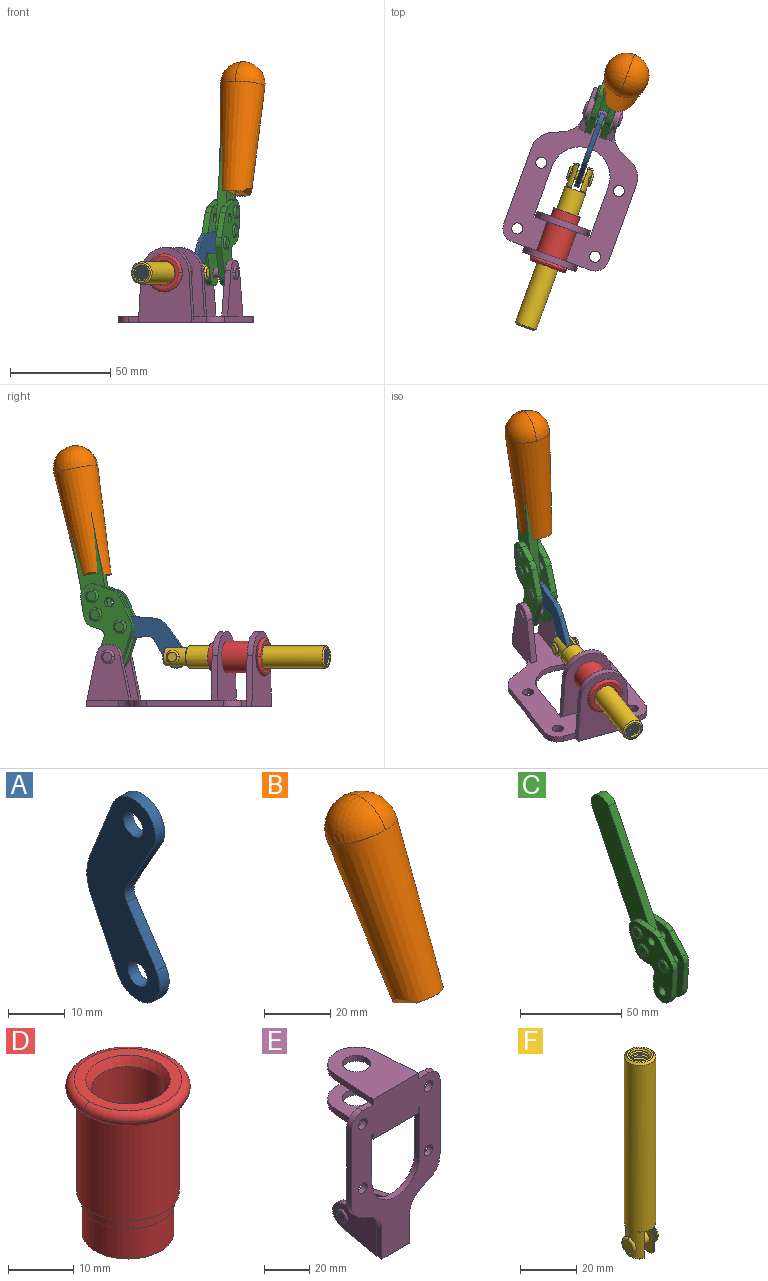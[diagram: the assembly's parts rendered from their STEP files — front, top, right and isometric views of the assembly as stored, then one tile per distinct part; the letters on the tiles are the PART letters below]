
ASSEMBLY  parts=6 mates=6
PART A: 12 faces, bbox 2.3x18.2x42.8 mm
  f0: cylinder r=2.4mm len=4.8mm, axis (1,0,0), area 34.9mm2, adj f4,f11
  f1: cylinder r=10.41mm len=8.47mm, axis (1,0,0), area 20.2mm2, adj f4,f9,f10,f11
  f2: cylinder r=3.05mm len=3.16mm, axis (1,0,0), area 7.7mm2, adj f4,f6,f7,f11
  f3: cylinder r=2.4mm len=4.8mm, axis (1,0,0), area 34.9mm2, adj f4,f11
  f4: plane 42.81x18.23mm, normal (-1,0,0), area 414.1mm2, adj f0,f1,f2,f3,f5,f6,f7,f8
  f5: cylinder r=5.54mm len=10.67mm, axis (1,0,0), area 41.8mm2, adj f4,f6,f10,f11
  f6: plane 11.66x6.53mm, normal (0,-0.87,-0.49), area 30.9mm2, adj f2,f4,f5,f11
  f7: plane 11.17x7.33mm, normal (0,-0.84,0.55), area 30.9mm2, adj f2,f4,f8,f11
  f8: cylinder r=5.54mm len=10.51mm, axis (1,0,0), area 41.8mm2, adj f4,f7,f9,f11
  f9: plane 13.67x6.67mm, normal (0,0.9,-0.44), area 35.1mm2, adj f1,f4,f8,f11
  f10: plane 14.1x5.7mm, normal (0,0.93,0.37), area 35.1mm2, adj f1,f4,f5,f11
  f11: plane 42.81x18.23mm, normal (1,0,0), area 414.1mm2, adj f0,f1,f2,f3,f5,f6,f7,f8
PART B: 11 faces, bbox 22.3x42.6x64.5 mm
  f0: sphere r=11.13mm, area 411.4mm2, adj f1,f8
  f1: cone r=11.11mm half-angle=3.3deg, axis (0,0.44,0.9), area 3251.8mm2, adj f0,f7,f8,f9,f10
  f2: cylinder r=6.16mm len=11.7mm, axis (1,0,0), area 89.5mm2, adj f3,f4,f5,f6
  f3: plane 60.23x36.75mm, normal (-1,0,0), area 763.6mm2, adj f2,f4,f6,f10
  f4: plane 51.37x25.05mm, normal (0,0.9,-0.44), area 264.2mm2, adj f2,f3,f5,f10
  f5: plane 60.23x36.75mm, normal (1,0,0), area 763.6mm2, adj f2,f4,f6,f10
  f6: plane 51.37x25.05mm, normal (0,-0.9,0.44), area 264.2mm2, adj f2,f3,f5,f10
  f7: plane 9.95x5.95mm, normal (0.71,-0.31,-0.64), area 25.8mm2, adj f1,f10
  f8: sphere r=11.13mm, area 411.4mm2, adj f0,f1
  f9: plane 9.95x5.95mm, normal (-0.71,-0.31,-0.64), area 25.8mm2, adj f1,f10
  f10: plane 14.27x11.38mm, normal (0,-0.44,-0.9), area 106.7mm2, adj f1,f3,f4,f5,f6,f7,f9
PART C: 59 faces, bbox 12.9x60.2x99.6 mm
  f0: torus R=2.39mm, axis (-1,0,0), area 14.9mm2, adj f20,f43,f51
  f1: torus R=2.39mm, axis (-1,0,0), area 14.9mm2, adj f19,f42,f51
  f2: torus R=2.39mm, axis (-1,0,0), area 14.9mm2, adj f18,f35,f51
  f3: torus R=2.39mm, axis (-1,0,0), area 14.9mm2, adj f14,f17,f23
  f4: torus R=2.39mm, axis (-1,0,0), area 14.9mm2, adj f13,f16,f23
  f5: torus R=2.39mm, axis (-1,0,0), area 14.9mm2, adj f12,f15,f23
  f6: cylinder r=2.39mm len=4.78mm, axis (1,0,0), area 46.5mm2, adj f48,f50,f51
  f7: cylinder r=2.39mm len=4.78mm, axis (1,0,0), area 46.5mm2, adj f50,f51
  f8: cylinder r=6.35mm len=12.68mm, axis (1,0,0), area 61.8mm2, adj f38,f39,f50,f51
  f9: cylinder r=2.39mm len=4.78mm, axis (-1,0,0), area 70.5mm2, adj f46,f50
  f10: cylinder r=2.39mm len=4.78mm, axis (-1,0,0), area 46.5mm2, adj f23,f45,f46
  f11: cylinder r=2.39mm len=4.78mm, axis (-1,0,0), area 46.5mm2, adj f23,f46
  f12: plane 4.78x4.78mm, normal (1,0,0), area 17.9mm2, adj f5,f15
  f13: plane 4.78x4.78mm, normal (1,0,0), area 17.9mm2, adj f4,f16
  f14: plane 4.78x4.78mm, normal (1,0,0), area 17.9mm2, adj f3,f17
  f15: torus R=2.39mm, axis (-1,0,0), area 14.9mm2, adj f5,f12,f23
  f16: torus R=2.39mm, axis (-1,0,0), area 14.9mm2, adj f4,f13,f23
  f17: torus R=2.39mm, axis (-1,0,0), area 14.9mm2, adj f3,f14,f23
  f18: plane 4.78x4.78mm, normal (-1,0,0), area 17.9mm2, adj f2,f35
  f19: plane 4.78x4.78mm, normal (-1,0,0), area 17.9mm2, adj f1,f42
  f20: plane 4.78x4.78mm, normal (-1,0,0), area 17.9mm2, adj f0,f43
  f21: plane 2.26x0.2mm, normal (1,0,0), area 0.2mm2, adj f31,f44
  f22: plane 2.26x0.2mm, normal (-1,0,0), area 0.2mm2, adj f41,f44
  f23: plane 39.37x30.77mm, normal (1,0,0), area 565.5mm2, adj f3,f4,f5,f10,f11,f15,f16,f17
  f24: cylinder r=6.1mm len=4.15mm, axis (-1,0,0), area 14.7mm2, adj f23,f25,f32,f46
  f25: plane 10.25x9.01mm, normal (0,-0.75,0.66), area 42.3mm2, adj f23,f24,f26,f46
  f26: cylinder r=6.35mm len=4.64mm, axis (-1,0,0), area 15.6mm2, adj f23,f25,f27,f46
  f27: plane 15.84x3.1mm, normal (0,-1,-0.07), area 49.2mm2, adj f23,f26,f28,f46
  f28: cylinder r=6.35mm len=12.68mm, axis (-1,0,0), area 61.8mm2, adj f23,f27,f29,f46
  f29: plane 8.11x3.1mm, normal (0,1,0.07), area 25.2mm2, adj f23,f28,f30,f46
  f30: cylinder r=3.05mm len=3.25mm, axis (-1,0,0), area 14.8mm2, adj f23,f29,f31,f46
  f31: plane 5.99x3.1mm, normal (0,0.07,-1), area 18.6mm2, adj f21,f23,f30,f44,f46
  f32: plane 9.5x3.1mm, normal (0,-0.07,1), area 29.5mm2, adj f23,f24,f33,f46,f47
  f33: cylinder r=6.1mm len=8.63mm, axis (-1,0,0), area 39.1mm2, adj f23,f32,f34,f47
  f34: plane 8.65x3.96mm, normal (0,0.91,-0.42), area 29.5mm2, adj f23,f33,f44,f47
  f35: torus R=2.39mm, axis (-1,0,0), area 14.9mm2, adj f2,f18,f51
  f36: plane 10.25x9.01mm, normal (0,-0.75,0.66), area 42.3mm2, adj f37,f49,f50,f51
  f37: cylinder r=6.35mm len=4.64mm, axis (1,0,0), area 15.6mm2, adj f36,f38,f50,f51
  f38: plane 15.84x3.1mm, normal (0,-1,-0.07), area 49.2mm2, adj f8,f37,f50,f51
  f39: plane 8.11x3.1mm, normal (0,1,0.07), area 25.2mm2, adj f8,f40,f50,f51
  f40: cylinder r=3.05mm len=3.25mm, axis (1,0,0), area 14.8mm2, adj f39,f41,f50,f51
  f41: plane 5.99x3.1mm, normal (0,0.07,-1), area 18.6mm2, adj f22,f40,f44,f50,f51
  f42: torus R=2.39mm, axis (-1,0,0), area 14.9mm2, adj f1,f19,f51
  f43: torus R=2.39mm, axis (-1,0,0), area 14.9mm2, adj f0,f20,f51
  f44: cylinder r=6.35mm len=12.12mm, axis (-1,0,0), area 128.9mm2, adj f21,f22,f23,f31,f34,f41,f46,f47
  f45: plane 2.65x1.35mm, normal (1,0,0), area 1mm2, adj f10,f55
  f46: plane 39.08x20.42mm, normal (-1,0,0), area 412.5mm2, adj f9,f10,f11,f24,f25,f26,f27,f28
  f47: plane 77.62x39.82mm, normal (1,0,0), area 850mm2, adj f32,f33,f34,f44,f53,f54,f55
  f48: plane 2.65x1.35mm, normal (-1,0,0), area 1mm2, adj f6,f55
  f49: cylinder r=6.1mm len=4.15mm, axis (1,0,0), area 14.7mm2, adj f36,f50,f51,f56
  f50: plane 39.08x20.42mm, normal (1,0,0), area 412.5mm2, adj f6,f7,f8,f9,f36,f37,f38,f39
  f51: plane 39.37x30.77mm, normal (-1,0,0), area 565.5mm2, adj f0,f1,f2,f6,f7,f8,f35,f36
  f52: plane 8.65x3.96mm, normal (0,0.91,-0.42), area 29.5mm2, adj f44,f51,f57,f58
  f53: plane 68.49x33.4mm, normal (0,0.9,-0.44), area 358.1mm2, adj f44,f47,f54,f58
  f54: cylinder r=6.35mm len=12.06mm, axis (1,0,0), area 93.7mm2, adj f47,f53,f55,f58
  f55: plane 68.49x33.4mm, normal (0,-0.9,0.44), area 358.1mm2, adj f44,f45,f46,f47,f48,f50,f54,f58
  f56: plane 9.5x3.1mm, normal (0,-0.07,1), area 29.5mm2, adj f49,f50,f51,f57,f58
  f57: cylinder r=6.1mm len=8.63mm, axis (1,0,0), area 39.1mm2, adj f51,f52,f56,f58
  f58: plane 77.62x39.82mm, normal (-1,0,0), area 850mm2, adj f44,f52,f53,f54,f55,f56,f57
PART D: 15 faces, bbox 20.6x20.6x28.7 mm
  f0: torus R=8.26mm, axis (0,0,1), area 56.8mm2, adj f1,f10,f12
  f1: torus R=8.26mm, axis (0,0,1), area 56.8mm2, adj f0,f6,f13
  f2: cylinder r=5.59mm len=25.91mm, axis (0,0,1), area 909.6mm2, adj f3,f4
  f3: cone r=6.86mm half-angle=45deg, axis (0,0,-1), area 70.2mm2, adj f2,f14
  f4: cone r=6.47mm half-angle=30deg, axis (0,0,1), area 66.7mm2, adj f2,f13
  f5: cylinder r=7.04mm len=14.07mm, axis (0,0,1), area 252.6mm2, adj f11,f14
  f6: torus R=8.26mm, axis (0,0,1), area 56.8mm2, adj f1,f12,f13
  f7: cylinder r=7.16mm len=14.33mm, axis (0,0,1), area 91.5mm2, adj f9,f11
  f8: cylinder r=7.86mm len=18.42mm, axis (0,0,1), area 909.6mm2, adj f9,f10
  f9: plane 15.72x15.72mm, normal (0,0,-1), area 33mm2, adj f7,f8
  f10: plane 16.51x16.51mm, normal (0,0,-1), area 19.9mm2, adj f0,f8,f12
  f11: plane 14.33x14.33mm, normal (0,0,-1), area 5.7mm2, adj f5,f7
  f12: torus R=8.26mm, axis (0,0,1), area 56.8mm2, adj f0,f6,f10
  f13: plane 16.51x16.51mm, normal (0,0,1), area 82.7mm2, adj f1,f4,f6
  f14: plane 14.07x14.07mm, normal (0,0,-1), area 7.8mm2, adj f3,f5
PART E: 55 faces, bbox 55.7x37.4x89.8 mm
  f0: torus R=2.41mm, axis (-1,0,0), area 15mm2, adj f11,f15,f25
  f1: torus R=2.41mm, axis (-1,0,0), area 15mm2, adj f10,f12,f22
  f2: cylinder r=2.78mm len=5.56mm, axis (0,-1,0), area 54.2mm2, adj f30,f54
  f3: cylinder r=14.99mm len=29.97mm, axis (0,-1,0), area 145.9mm2, adj f30,f49,f53,f54
  f4: cylinder r=2.78mm len=5.56mm, axis (0,-1,0), area 54.2mm2, adj f30,f54
  f5: cylinder r=2.78mm len=5.56mm, axis (0,-1,0), area 54.2mm2, adj f30,f54
  f6: cylinder r=2.78mm len=5.56mm, axis (0,-1,0), area 54.2mm2, adj f30,f54
  f7: cylinder r=6.35mm len=12.7mm, axis (0,0,1), area 123.6mm2, adj f27,f51
  f8: cylinder r=6.35mm len=12.7mm, axis (0,0,-1), area 124.7mm2, adj f21,f35
  f9: cylinder r=2.41mm len=11.18mm, axis (-1,0,0), area 169.4mm2, adj f16,f19
  f10: plane 4.83x4.83mm, normal (1,0,0), area 18.3mm2, adj f1,f12
  f11: plane 4.83x4.83mm, normal (-1,0,0), area 18.3mm2, adj f0,f15
  f12: torus R=2.41mm, axis (-1,0,0), area 15mm2, adj f1,f10,f22
  f13: cylinder r=6.35mm len=12.41mm, axis (1,0,0), area 53.4mm2, adj f18,f19,f22,f23
  f14: cylinder r=6.35mm len=12.41mm, axis (-1,0,0), area 53.4mm2, adj f16,f17,f24,f25
  f15: torus R=2.41mm, axis (-1,0,0), area 15mm2, adj f0,f11,f25
  f16: plane 27.86x22.35mm, normal (1,0,0), area 425.4mm2, adj f9,f14,f17,f24,f30
  f17: plane 22.86x4.97mm, normal (0,0.21,0.98), area 72.5mm2, adj f14,f16,f25,f30
  f18: plane 22.86x4.97mm, normal (0,0.21,0.98), area 72.5mm2, adj f13,f19,f22,f30
  f19: plane 27.86x22.35mm, normal (-1,0,0), area 425.4mm2, adj f9,f13,f18,f23,f30
  f20: cylinder r=12.7mm len=25.35mm, axis (0,0,-1), area 119.8mm2, adj f21,f34,f35,f36
  f21: plane 34.21x28.07mm, normal (0,0,-1), area 702.4mm2, adj f8,f20,f30,f34,f36
  f22: plane 27.96x22.45mm, normal (1,0,0), area 407.2mm2, adj f1,f12,f13,f18,f23,f30,f42,f43
  f23: plane 22.86x4.97mm, normal (0,0.21,-0.98), area 72.5mm2, adj f13,f19,f22,f44
  f24: plane 22.86x4.97mm, normal (0,0.21,-0.98), area 72.5mm2, adj f14,f16,f25,f44
  f25: plane 27.86x22.35mm, normal (-1,0,0), area 407.1mm2, adj f0,f14,f15,f17,f24,f30,f45,f46
  f26: plane 3.1x0.95mm, normal (0,0,-1), area 2.7mm2, adj f30,f49,f50,f54
  f27: plane 34.21x28.07mm, normal (0,0,1), area 702.4mm2, adj f7,f28,f30,f50,f52
  f28: cylinder r=12.7mm len=25.35mm, axis (0,0,1), area 118.8mm2, adj f27,f50,f51,f52
  f29: plane 3.1x0.95mm, normal (0,0,-1), area 2.7mm2, adj f30,f52,f53,f54
  f30: plane 86.54x55.63mm, normal (0,1,0), area 2362.9mm2, adj f2,f3,f4,f5,f6,f16,f17,f18
  f31: plane 40.56x3.1mm, normal (-1,0,0), area 125.7mm2, adj f30,f32,f48,f54
  f32: cylinder r=7.11mm len=7.11mm, axis (0,-1,0), area 34.6mm2, adj f30,f31,f33,f54
  f33: plane 6.67x3.1mm, normal (0,0,1), area 20.4mm2, adj f30,f32,f34,f54
  f34: plane 25.39x3.13mm, normal (-1,0.06,0), area 79.5mm2, adj f20,f21,f33,f35,f54
  f35: plane 37.31x28.45mm, normal (0,0,1), area 789.9mm2, adj f8,f20,f34,f36,f54
  f36: plane 25.39x3.13mm, normal (1,0.06,0), area 79.5mm2, adj f20,f21,f35,f37,f54
  f37: plane 6.67x3.1mm, normal (0,0,1), area 20.4mm2, adj f30,f36,f38,f54
  f38: cylinder r=7.11mm len=7.11mm, axis (0,-1,0), area 34.6mm2, adj f30,f37,f39,f54
  f39: plane 40.56x3.1mm, normal (1,0,0), area 125.7mm2, adj f30,f38,f40,f54
  f40: cylinder r=11.18mm len=10.16mm, axis (0,-1,0), area 39.5mm2, adj f30,f39,f41,f54
  f41: plane 6.09x3.1mm, normal (0.42,0,-0.91), area 20.8mm2, adj f30,f40,f42,f54
  f42: cylinder r=11.18mm len=9.41mm, axis (0,-1,0), area 37.2mm2, adj f22,f30,f41,f43,f54
  f43: plane 16.5x3.1mm, normal (1,0,0), area 51.1mm2, adj f22,f42,f44,f54
  f44: plane 17.37x3.1mm, normal (0,0,-1), area 53.8mm2, adj f23,f24,f30,f43,f45,f54
  f45: plane 16.5x3.1mm, normal (-1,0,0), area 51.1mm2, adj f25,f44,f46,f54
  f46: cylinder r=11.18mm len=9.41mm, axis (0,-1,0), area 37.2mm2, adj f25,f30,f45,f47,f54
  f47: plane 6.09x3.1mm, normal (-0.42,0,-0.91), area 20.8mm2, adj f30,f46,f48,f54
  f48: cylinder r=11.18mm len=10.16mm, axis (0,-1,0), area 39.5mm2, adj f30,f31,f47,f54
  f49: plane 26.54x3.1mm, normal (-1,0,0), area 82.3mm2, adj f3,f26,f30,f54
  f50: plane 25.39x3.1mm, normal (1,0.06,0), area 78.8mm2, adj f26,f27,f28,f51,f54
  f51: plane 37.31x28.45mm, normal (0,0,-1), area 789.9mm2, adj f7,f28,f50,f52,f54
  f52: plane 25.39x3.1mm, normal (-1,0.06,0), area 78.8mm2, adj f27,f28,f29,f51,f54
  f53: plane 26.54x3.1mm, normal (1,0,0), area 82.3mm2, adj f3,f29,f30,f54
  f54: plane 89.66x55.63mm, normal (0,-1,0), area 2678.5mm2, adj f2,f3,f4,f5,f6,f26,f29,f31
PART F: 48 faces, bbox 12.6x11.1x86.1 mm
  f0: torus R=2.41mm, axis (-1,0,0), area 15mm2, adj f30,f32,f34
  f1: torus R=2.41mm, axis (-1,0,0), area 15mm2, adj f29,f31,f33
  f2: cylinder r=5.54mm len=72.39mm, axis (0,0,1), area 2518.5mm2, adj f3,f4,f42,f43
  f3: cone r=5.54mm half-angle=45deg, axis (0,0,1), area 7.6mm2, adj f2,f5,f41
  f4: cone r=5.54mm half-angle=45deg, axis (0,0,-1), area 34.9mm2, adj f2,f39
  f5: cylinder r=5.08mm len=11.48mm, axis (0,0,1), area 108.3mm2, adj f3,f7,f8,f41
  f6: cylinder r=2.41mm len=4.83mm, axis (-1,0,0), area 71.2mm2, adj f40,f41
  f7: cylinder r=2.41mm len=4.83mm, axis (-1,0,0), area 7.6mm2, adj f5,f34
  f8: cone r=5.08mm half-angle=45deg, axis (0,0,1), area 10.6mm2, adj f5,f37,f41
  f9: cone r=3.98mm half-angle=45deg, axis (0,0,1), area 17.6mm2, adj f27,f39,f45,f46,f47
  f10: cylinder r=2.41mm len=4.83mm, axis (-1,0,0), area 7.6mm2, adj f33,f38
  f11: cylinder r=3.2mm len=6.4mm, axis (0,0,1), area 78.4mm2, adj f12,f28,f44,f45,f47
  f12: cylinder r=3.2mm len=6.4mm, axis (0,0,1), area 10.5mm2, adj f11,f13,f45,f47
  f13: cylinder r=3.2mm len=6.4mm, axis (0,0,1), area 10.5mm2, adj f12,f14,f45,f47
  f14: cylinder r=3.2mm len=6.4mm, axis (0,0,1), area 10.5mm2, adj f13,f15,f45,f47
  f15: cylinder r=3.2mm len=6.4mm, axis (0,0,1), area 10.5mm2, adj f14,f16,f45,f47
  f16: cylinder r=3.2mm len=6.4mm, axis (0,0,1), area 10.5mm2, adj f15,f17,f45,f47
  f17: cylinder r=3.2mm len=6.4mm, axis (0,0,1), area 10.5mm2, adj f16,f18,f45,f47
  f18: cylinder r=3.2mm len=6.4mm, axis (0,0,1), area 10.5mm2, adj f17,f19,f45,f47
  f19: cylinder r=3.2mm len=6.4mm, axis (0,0,1), area 10.5mm2, adj f18,f20,f45,f47
  f20: cylinder r=3.2mm len=6.4mm, axis (0,0,1), area 10.5mm2, adj f19,f21,f45,f47
  f21: cylinder r=3.2mm len=6.4mm, axis (0,0,1), area 10.5mm2, adj f20,f22,f45,f47
  f22: cylinder r=3.2mm len=6.4mm, axis (0,0,1), area 10.5mm2, adj f21,f23,f45,f47
  f23: cylinder r=3.2mm len=6.4mm, axis (0,0,1), area 10.5mm2, adj f22,f24,f45,f47
  f24: cylinder r=3.2mm len=6.4mm, axis (0,0,1), area 10.5mm2, adj f23,f25,f45,f47
  f25: cylinder r=3.2mm len=6.4mm, axis (0,0,1), area 10.5mm2, adj f24,f26,f45,f47
  f26: cylinder r=3.2mm len=6.4mm, axis (0,0,1), area 10.5mm2, adj f25,f27,f45,f47
  f27: cylinder r=3.2mm len=6.4mm, axis (0,0,1), area 7.4mm2, adj f9,f26,f45,f47
  f28: cone r=3.2mm half-angle=60deg, axis (0,0,1), area 37.2mm2, adj f11
  f29: plane 4.83x4.83mm, normal (-1,0,0), area 18.3mm2, adj f1,f31
  f30: plane 4.83x4.83mm, normal (1,0,0), area 18.3mm2, adj f0,f32
  f31: torus R=2.41mm, axis (-1,0,0), area 15mm2, adj f1,f29,f33
  f32: torus R=2.41mm, axis (-1,0,0), area 15mm2, adj f0,f30,f34
  f33: plane 6.83x6.83mm, normal (1,0,0), area 18.3mm2, adj f1,f10,f31
  f34: plane 6.83x6.83mm, normal (-1,0,0), area 18.3mm2, adj f0,f7,f32
  f35: cone r=5.08mm half-angle=45deg, axis (0,0,1), area 10.6mm2, adj f36,f38,f40
  f36: plane 7.25x1.97mm, normal (0,0,-1), area 10mm2, adj f35,f40
  f37: plane 7.25x1.97mm, normal (0,0,-1), area 10mm2, adj f8,f41
  f38: cylinder r=5.08mm len=11.48mm, axis (0,0,1), area 108.3mm2, adj f10,f35,f40,f42
  f39: plane 9.55x9.55mm, normal (0,0,1), area 22mm2, adj f4,f9
  f40: plane 12.76x10.09mm, normal (1,0,0), area 95.7mm2, adj f6,f35,f36,f38,f42,f43
  f41: plane 12.76x10.09mm, normal (-1,0,0), area 95.7mm2, adj f3,f5,f6,f8,f37,f43
  f42: cone r=5.54mm half-angle=45deg, axis (0,0,1), area 7.6mm2, adj f2,f38,f40
  f43: plane 11.07x4.7mm, normal (0,0,-1), area 50.4mm2, adj f2,f40,f41
  f44: plane 0.89x0.62mm, normal (-1,0,0), area 0.3mm2, adj f11,f45,f46,f47
  f45: bspline ~24.8x7.63mm, area 266.6mm2, adj f9,f11,f12,f13,f14,f15,f16,f17
  f46: bspline ~24.87x7.63mm, area 73.6mm2, adj f9,f44,f45,f47
  f47: bspline ~24.98x7.63mm, area 272.5mm2, adj f9,f11,f12,f13,f14,f15,f16,f17
PLACE A rot(axis=(0.09,0.53,0.85),163deg) t=(31.71,29.07,7.7)mm
PLACE B rot(axis=(0.59,-0.1,-0.8),25deg) t=(27.91,5.01,46.24)mm
PLACE C rot(axis=(0.59,-0.1,-0.8),25deg) t=(23.53,6.61,46.24)mm
PLACE D rot(axis=(0.97,-0.17,-0.17),91.7deg) t=(23.53,6.59,-3)mm
PLACE E rot(axis=(0.97,-0.17,-0.17),91.7deg) t=(23.53,6.59,-3)mm fixed
PLACE F rot(axis=(0.97,-0.17,-0.17),91.7deg) t=(28.46,20.14,-3)mm
MATE revolute C.f7 <-> E.f0  axis (-0.94,0.34,0) through (34.51,36.75,21.61)mm
MATE fastened B.f2 <-> C.f54  axis (0.94,-0.34,0) through (44.36,56.96,117.53)mm
MATE fastened D.f2 <-> E.f7  axis (0.34,0.94,0) through (7.66,-37,21.61)mm
MATE revolute A.f3 <-> F.f6  axis (-0.94,0.34,0) through (23.17,5.6,21.61)mm
MATE slider F.f2 <-> D.f2  axis (-0.34,-0.94,0) through (8.36,-35.09,21.61)mm
MATE revolute A.f5 <-> C.f4  axis (-0.94,0.34,0) through (32.74,31.89,36.62)mm
